annotation { "Feature Type Name" : "Feature", "Feature Type Description" : "" }
export const myFeature = defineFeature(function(context is Context, id is Id, definition is map)
    precondition{}
    {
        {
            var Q0;
            Q0=qCreatedBy(makeId("Right.planeOp"),FACE);
            var sketch = newSketch(context, id + "F0", { "sketchPlane" : qUnion([Q0])});
            skFitSpline(sketch, "E0", {"points": [v(-53.55, -63.5) * mm, v(17.07, -40.74) * mm, v(41.37, 24.98) * mm, v(-40.87, 13.99) * mm, v(-45.75, 42.22) * mm, v(23.13, 54.35) * mm], "startDerivative": vector(334.8, 0) * mm, "endDerivative": vector(263.82, -130.35) * mm});
            skLineSegment(sketch, "E1", {"start": v(23.13, 54.35) * mm, "end": v(23.13, 71.15) * mm});
            skLineSegment(sketch, "E2", {"start": v(23.13, 71.15) * mm, "end": v(-71.07, 71.15) * mm});
            skLineSegment(sketch, "E3", {"start": v(-71.07, 71.15) * mm, "end": v(-71.07, -63.5) * mm});
            skLineSegment(sketch, "E4", {"start": v(-71.07, -63.5) * mm, "end": v(-53.55, -63.5) * mm});
            skSolve(sketch);
        }
        {
            var Q0;
            Q0 = qSketchRegion(id + "F0", true);
            extrude(context, id + "F1", {"entities" : qUnion([Q0]), "depth" : 30 * mm, "hasDraft" : true, "draftAngle" : 3 * degree, "draftPullDirection" : true, "hasSecondDirection" : true, "secondDirectionOppositeDirection" : true, "secondDirectionDepth" : 50 * mm, "hasSecondDirectionDraft" : true, "secondDirectionDraftAngle" : 3 * degree});
        }
        {
            var Q0;
            Q0=makeQuery(id+"F1.opExtrude","CAP_FACE",FACE,{"disambiguationData":[OSD([sQuery(id+"F0.wireOp",EDGE,"E0"),sQuery(id+"F0.wireOp",EDGE,"E1"),sQuery(id+"F0.wireOp",EDGE,"E2"),sQuery(id+"F0.wireOp",EDGE,"E3"),sQuery(id+"F0.wireOp",EDGE,"E4")])],"isStart":false});
            var sketch = newSketch(context, id + "F2", { "sketchPlane" : qUnion([Q0])});
            skCircle(sketch, "E5", {"center": v(5.15, -4.83) * mm, "radius": 7.97 * mm});
            skCircle(sketch, "E6.cCircle", {"center": v(-38.85, -30.23) * mm, "radius": 13.9 * mm, "construction": true});
            skLineSegment(sketch, "E6.0", {"start": v(-26.8, -37.19) * mm, "end": v(-38.85, -44.14) * mm});
            skLineSegment(sketch, "E6.1", {"start": v(-38.85, -44.14) * mm, "end": v(-50.89, -37.19) * mm});
            skLineSegment(sketch, "E6.2", {"start": v(-50.89, -37.19) * mm, "end": v(-50.89, -23.28) * mm});
            skLineSegment(sketch, "E6.3", {"start": v(-50.89, -23.28) * mm, "end": v(-38.85, -16.33) * mm});
            skLineSegment(sketch, "E6.4", {"start": v(-38.85, -16.33) * mm, "end": v(-26.8, -23.28) * mm});
            skLineSegment(sketch, "E6.5", {"start": v(-26.8, -23.28) * mm, "end": v(-26.8, -37.19) * mm});
            skLineSegment(sketch, "E7", {"start": v(-38.85, -30.23) * mm, "end": v(5.15, -4.83) * mm});
            skSolve(sketch);
        }
        {
            var Q0;
            Q0 = qSketchRegion(id + "F2", true);
            extrude(context, id + "F3", {"entities" : qUnion([Q0]), "operationType" : NewBodyOperationType.REMOVE, "endBound" : BoundingType.THROUGH_ALL, "oppositeDirection" : true, "depth" : 25.4 * mm, "hasDraft" : true, "draftAngle" : 0.5 * degree, "draftPullDirection" : true});
        }
        {
            var Q0;
            Q0=makeQuery(id+"F1.opExtrude","CAP_FACE",FACE,{"disambiguationData":[OSD([sQuery(id+"F0.wireOp",EDGE,"E0"),sQuery(id+"F0.wireOp",EDGE,"E1"),sQuery(id+"F0.wireOp",EDGE,"E2"),sQuery(id+"F0.wireOp",EDGE,"E3"),sQuery(id+"F0.wireOp",EDGE,"E4")])],"isStart":true});
            shell(context, id + "F4", {"entities" : qUnion([Q0]), "thickness" : 2.5 * mm});
        }
        {
            var Q0;
            {var subQ0=makeQuery(id+"F1.opExtrude","SWEPT_FACE",FACE,{"disambiguationData":[OSD([sQuery(id+"F0.wireOp",EDGE,"E2")])]});Q0=makeQuery(id+"F1.booleanUnion0.opBoolean","MERGE",FACE,{"derivedFrom":[makeQuery(id+"F1.split0.splitOp","SPLIT",FACE,{"derivedFrom":subQ0}),makeQuery(id+"F1.split0.splitOp","SPLIT",FACE,{"derivedFrom":subQ0,"isFromBackBody":true})]});}
            var sketch = newSketch(context, id + "F5", { "sketchPlane" : qUnion([Q0])});
            skText(sketch, "E8", { "text": "Impressive System", "fontName": "OpenSans-BoldItalic.ttf"});
            const initialGuessF5  = {"E8": [-0.04506, -0.06276, 0, 1, 0.00413]};
            skSetInitialGuess(sketch, initialGuessF5);
            skSolve(sketch);
        }
        {
            var Q0;
            Q0=makeQuery(id+"F5.imprint","IMPRINT",FACE,{"disambiguationData":[TD([[makeQuery(id+"F5.imprint","IMPRINT",EDGE,{"derivedFrom":sQuery(id+"F5.wireOp",EDGE,"E8.sketch_text.stroke-0")}),1.0]])]});
            var sketch = newSketch(context, id + "F6", { "sketchPlane" : qUnion([Q0])});
            skText(sketch, "E9", { "text": "Nice Job", "fontName": "OpenSans-BoldItalic.ttf"});
            const initialGuessF6  = {"E9": [0.02142, -0.00717, 0, 1, 0.00471]};
            skSetInitialGuess(sketch, initialGuessF6);
            skSolve(sketch);
        }
        {
            var Q0;
            Q0 = qSketchRegion(id + "F5", true);
            extrude(context, id + "F7", {"entities" : qUnion([Q0]), "operationType" : NewBodyOperationType.ADD, "depth" : 1.5 * mm});
        }
        {
            var Q0;
            Q0 = qSketchRegion(id + "F6", true);
            extrude(context, id + "F8", {"entities" : qUnion([Q0]), "operationType" : NewBodyOperationType.REMOVE, "oppositeDirection" : true, "depth" : 1.5 * mm});
        }
    });